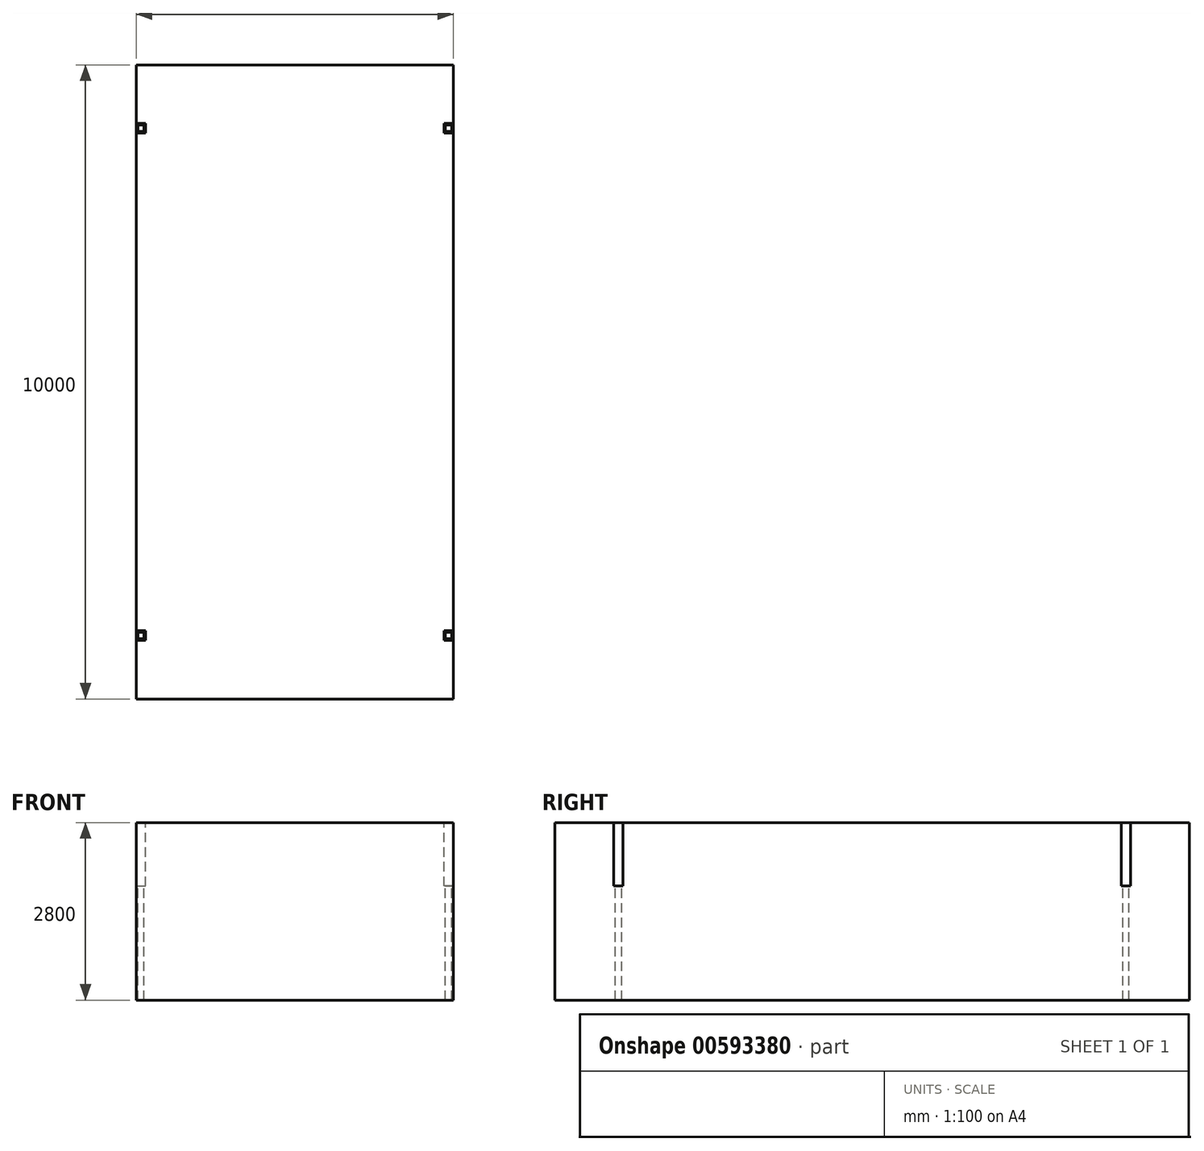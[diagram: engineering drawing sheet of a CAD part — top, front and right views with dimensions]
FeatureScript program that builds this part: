
annotation { "Feature Type Name" : "Feature", "Feature Type Description" : "" }
export const myFeature = defineFeature(function(context is Context, id is Id, definition is map)
    precondition{}
    {
        {
            var Q0;
            Q0=qCreatedBy(makeId("Top.planeOp"),FACE);
            var sketch = newSketch(context, id + "F0", { "sketchPlane" : qUnion([Q0])});
            skLineSegment(sketch, "E0.bottom", {"start": v(-2446.59, 5095.64) * mm, "end": v(2553.41, 5095.64) * mm});
            skLineSegment(sketch, "E0.top", {"start": v(-2446.59, -4904.36) * mm, "end": v(2553.41, -4904.36) * mm});
            skLineSegment(sketch, "E0.left", {"start": v(-2446.59, 5095.64) * mm, "end": v(-2446.59, -4904.36) * mm});
            skLineSegment(sketch, "E0.right", {"start": v(2553.41, 5095.64) * mm, "end": v(2553.41, -4904.36) * mm});
            skSolve(sketch);
        }
        {
            var Q0;
            Q0 = qSketchRegion(id + "F0", true);
            extrude(context, id + "F1", {"entities" : qUnion([Q0]), "depth" : 2800 * mm, "offsetDistance" : 25 * mm});
        }
        {
            var Q0;
            Q0=makeQuery(id+"F1.opExtrude","CAP_FACE",FACE,{"disambiguationData":[OSD([sQuery(id+"F0.wireOp",EDGE,"E0.bottom"),sQuery(id+"F0.wireOp",EDGE,"E0.top"),sQuery(id+"F0.wireOp",EDGE,"E0.left"),sQuery(id+"F0.wireOp",EDGE,"E0.right")])],"isStart":false});
            var sketch = newSketch(context, id + "F2", { "sketchPlane" : qUnion([Q0])});
            skLineSegment(sketch, "E1.bottom", {"start": v(-2446.59, 4170.64) * mm, "end": v(-2296.59, 4170.64) * mm});
            skLineSegment(sketch, "E1.top", {"start": v(-2446.59, 4020.64) * mm, "end": v(-2296.59, 4020.64) * mm});
            skLineSegment(sketch, "E1.left", {"start": v(-2446.59, 4170.64) * mm, "end": v(-2446.59, 4020.64) * mm});
            skLineSegment(sketch, "E1.right", {"start": v(-2296.59, 4170.64) * mm, "end": v(-2296.59, 4020.64) * mm});
            skLineSegment(sketch, "E2.bottom", {"start": v(2553.41, 4020.64) * mm, "end": v(2403.41, 4020.64) * mm});
            skLineSegment(sketch, "E2.top", {"start": v(2553.41, 4170.64) * mm, "end": v(2403.41, 4170.64) * mm});
            skLineSegment(sketch, "E2.left", {"start": v(2553.41, 4020.64) * mm, "end": v(2553.41, 4170.64) * mm});
            skLineSegment(sketch, "E2.right", {"start": v(2403.41, 4020.64) * mm, "end": v(2403.41, 4170.64) * mm});
            skLineSegment(sketch, "E3.bottom", {"start": v(2553.41, -3979.36) * mm, "end": v(2403.41, -3979.36) * mm});
            skLineSegment(sketch, "E3.top", {"start": v(2553.41, -3829.36) * mm, "end": v(2403.41, -3829.36) * mm});
            skLineSegment(sketch, "E3.left", {"start": v(2553.41, -3979.36) * mm, "end": v(2553.41, -3829.36) * mm});
            skLineSegment(sketch, "E3.right", {"start": v(2403.41, -3979.36) * mm, "end": v(2403.41, -3829.36) * mm});
            skLineSegment(sketch, "E4.bottom", {"start": v(-2446.59, -3829.36) * mm, "end": v(-2296.59, -3829.36) * mm});
            skLineSegment(sketch, "E4.top", {"start": v(-2446.59, -3979.36) * mm, "end": v(-2296.59, -3979.36) * mm});
            skLineSegment(sketch, "E4.left", {"start": v(-2446.59, -3829.36) * mm, "end": v(-2446.59, -3979.36) * mm});
            skLineSegment(sketch, "E4.right", {"start": v(-2296.59, -3829.36) * mm, "end": v(-2296.59, -3979.36) * mm});
            skSolve(sketch);
        }
        {
            var Q0;
            Q0 = qSketchRegion(id + "F2", true);
            extrude(context, id + "F3", {"entities" : qUnion([Q0]), "operationType" : NewBodyOperationType.REMOVE, "oppositeDirection" : true, "depth" : 1000 * mm, "offsetDistance" : 25 * mm});
        }
        {
            var Q0;
            Q0=makeQuery(id+"F3.boolean.opBoolean","COPY",FACE,{"derivedFrom":makeQuery(id+"F3.opExtrude","CAP_FACE",FACE,{"disambiguationData":[OSD([sQuery(id+"F2.wireOp",EDGE,"E2.bottom"),sQuery(id+"F2.wireOp",EDGE,"E2.top"),sQuery(id+"F2.wireOp",EDGE,"E2.left"),sQuery(id+"F2.wireOp",EDGE,"E2.right")])],"isStart":false})});
            var sketch = newSketch(context, id + "F4", { "sketchPlane" : qUnion([Q0])});
            skLineSegment(sketch, "E5.bottom", {"start": v(2428.41, 4045.64) * mm, "end": v(2528.41, 4045.64) * mm});
            skLineSegment(sketch, "E5.top", {"start": v(2428.41, 4145.64) * mm, "end": v(2528.41, 4145.64) * mm});
            skLineSegment(sketch, "E5.left", {"start": v(2428.41, 4045.64) * mm, "end": v(2428.41, 4145.64) * mm});
            skLineSegment(sketch, "E5.right", {"start": v(2528.41, 4045.64) * mm, "end": v(2528.41, 4145.64) * mm});
            skLineSegment(sketch, "E6.bottom", {"start": v(-2421.59, 4045.64) * mm, "end": v(-2321.59, 4045.64) * mm});
            skLineSegment(sketch, "E6.top", {"start": v(-2421.59, 4145.64) * mm, "end": v(-2321.59, 4145.64) * mm});
            skLineSegment(sketch, "E6.left", {"start": v(-2421.59, 4045.64) * mm, "end": v(-2421.59, 4145.64) * mm});
            skLineSegment(sketch, "E6.right", {"start": v(-2321.59, 4045.64) * mm, "end": v(-2321.59, 4145.64) * mm});
            skLineSegment(sketch, "E7.bottom", {"start": v(-2421.59, -3954.36) * mm, "end": v(-2321.59, -3954.36) * mm});
            skLineSegment(sketch, "E7.top", {"start": v(-2421.59, -3854.36) * mm, "end": v(-2321.59, -3854.36) * mm});
            skLineSegment(sketch, "E7.left", {"start": v(-2421.59, -3954.36) * mm, "end": v(-2421.59, -3854.36) * mm});
            skLineSegment(sketch, "E7.right", {"start": v(-2321.59, -3954.36) * mm, "end": v(-2321.59, -3854.36) * mm});
            skLineSegment(sketch, "E8.bottom", {"start": v(2428.41, -3954.36) * mm, "end": v(2528.41, -3954.36) * mm});
            skLineSegment(sketch, "E8.top", {"start": v(2428.41, -3854.36) * mm, "end": v(2528.41, -3854.36) * mm});
            skLineSegment(sketch, "E8.left", {"start": v(2428.41, -3954.36) * mm, "end": v(2428.41, -3854.36) * mm});
            skLineSegment(sketch, "E8.right", {"start": v(2528.41, -3954.36) * mm, "end": v(2528.41, -3854.36) * mm});
            skSolve(sketch);
        }
        {
            var Q0;
            Q0 = qSketchRegion(id + "F4", true);
            extrude(context, id + "F5", {"entities" : qUnion([Q0]), "operationType" : NewBodyOperationType.REMOVE, "oppositeDirection" : true, "depth" : 1800 * mm, "offsetDistance" : 25 * mm});
        }
    });
